# Revit family: IS_Tempo_Multiproduct_BIM_ES_E3240;E3242
name_source: partatom
category: Plumbing Fixtures
revit_build: Autodesk Revit 2017 (Build: 20160225_1515(x64)
units: mm (PartAtom-declared; Revit-internal decimal feet)

## family parameters
Cut with Voids When Loaded = No
Host = Face
OmniClass Number = 23.45.05.14.21.11
OmniClass Title = Bath/Shower Units
Part Type = Normal
Room Calculation Point = No
Round Connector Dimension = Use Diameter
Shared = Yes

## types (4) — shared parameters
Accesorios = https://www.idealstandard.es
AlturaNominal = 615 mm
AnchuraNominal = 500 mm
Assembly Code = C1030200
Autor = Ideal Standard Iberia
Ayuda = https://www.idealstandard.es
BREEAM = No
ChromeHandle = IS_IdealStandard_Fitting_Chrome_Render
Default Elevation = 900 mm
DescripciónUniclass2015 = Wall-hung wash basins
Espacio = Interno
Forma = Rectangular
GarantíaDeLasPiezas = 2
GarantíaPiezas = 2
GuíaDeInstallación = https://www.idealstandard.es
IfcExportaComo = IfcFurnitureType
InformaciónDeProducto = https://www.idealstandard.es
LongitudNominal = 500 mm
Maneta = No
Manufacturer = https://www.idealstandard.es
Marca = Ideal Standard Iberia
MontajeDeLavabo = A Pared
NBSDescription = Bathroom integrated duct work
NBSReference = 45-35-72/320
PlatoDeDucha = No
ProfundidadNominal = 500 mm
ReferenciaUniclass2015 = Pr_40_20_96_96
Repuestos = https://www.idealstandard.es
Revisión = 1
Teléfono = +34 93 561 80 00
TestDePresión = 10 Bar
TipoDeConexión = Mechanical
TipoDeExportaciónIfc = BATHROOMCABINET
TipoDeGarantía = Garantía del fabricante
URL = https://www.idealstandard.es
Uniclass2015Description = Bathroom cabinets
Uniclass2015Reference = Pr_40_30_78_03
UnidadDeTiempo = Años
UnidadDeVolúmen = Litros
UnidadDeÁrea = milimetros
UnidadGarantía = Años
UnidadLineal = milimetros
UnidadMonetaria = €
UrlDelFabricante = https://www.idealstandard.es
Versión = 1
VersiónUniclass2015 = v1.1
WRAS = No
WaterEfficientProduct = No
ÁreaDeMedición = Interna
zero-valued in all types: Cost, DiámetroDeDesagüe, GrosorDelMaterial, NivelDeDesbordamiento, PesoBruto

## per-type parameters (varying)
| type | Acabado | CódigoDeBarras | Description | Destacado | Dimensiones | HandleDistance | LaminateFinish | Model | Nombre | NombreDeObjetoBim | NúmeroDeModelo | PesoNeto | Referencia | ReferenciaDeModelo |
| E3240SG - Tempo 600mm Wall-mounted Vanity Basin Unit - Two Drawers - Sandy Grey | Sandy grey | 5017830475644 | MUEBLE TEMPO 60CM CON CAJONES BLANCO | MUEBLE TEMPO 60CM CON CAJONES BLANCO | 440 x 500 x 600 mm | 150 mm | IS_IdealStandard_Laminate_SandyGrey_SG_Render | E3240SG | IS_IdealStandard_Wall-hung wash basins_ULYSSE-GEMMA2-TEMPO_E3240 | Wall-hung wash basins_ULYSSE-GEMMA2-TEMPO_E3240_IdealStandard | E3240SG | 19,95 | E3240SG | MUEBLE TEMPO 60CM CON CAJONES BLANCO |
| E3242SG - Tempo 800mm Wall-mounted Vanity Basin Unit - Two Drawers - Sandy Grey | Sandy grey | 5017830475705 | MUEBLE TEMPO 80CM CON CAJONES BLANCO | MUEBLE TEMPO 80CM CON CAJONES BLANCO | 440 x 500 x 800 mm | 250 mm | IS_IdealStandard_Laminate_SandyGrey_SG_Render | E3242SG | IS_IdealStandard_Wall-hung wash basins_ULYSSE-GEMMA2-TEMPO_E3242 | Wall-hung wash basins_ULYSSE-GEMMA2-TEMPO_E3242_IdealStandard | E3242SG | 23,30 | E3242SG | MUEBLE TEMPO 80CM CON CAJONES BLANCO |
| E3240WG - Tempo 600mm Wall-mounted Vanity Basin Unit - Two Drawers – White Gloss | Blanco Brillante | 5017830475651 | MUEBLE TEMPO 60CM CON CAJONES BLANCO | MUEBLE TEMPO 60CM CON CAJONES BLANCO | 440 x 500 x 600 mm | 150 mm | IS_IdealStandard_Laminate_White_WG_Render | E3240WG | IS_IdealStandard_Wall-hung wash basins_TESI_E3240 | Wall-hung wash basins_TESI_E3240_IdealStandard | E3240WG | 19,95 | E3240WG | MUEBLE TEMPO 60CM CON CAJONES BLANCO |
| E3242WG - Tempo 800mm Wall-mounted Vanity Basin Unit - Two Drawers – White Gloss | Blanco Brillante | 5017830475712 | MUEBLE TEMPO 80CM CON CAJONES BLANCO | MUEBLE TEMPO 80CM CON CAJONES BLANCO | 440 x 500 x 800 mm | 250 mm | IS_IdealStandard_Laminate_White_WG_Render | E3242WG | IS_IdealStandard_Wall-hung wash basins_TESI_E3242 | Wall-hung wash basins_TESI_E3242_IdealStandard | E3242WG | 23,30 | E3242WG | MUEBLE TEMPO 80CM CON CAJONES BLANCO |

## geometry (parser evidence)
native form markers: Sweep x2
no freeform markers — native parametric forms only
